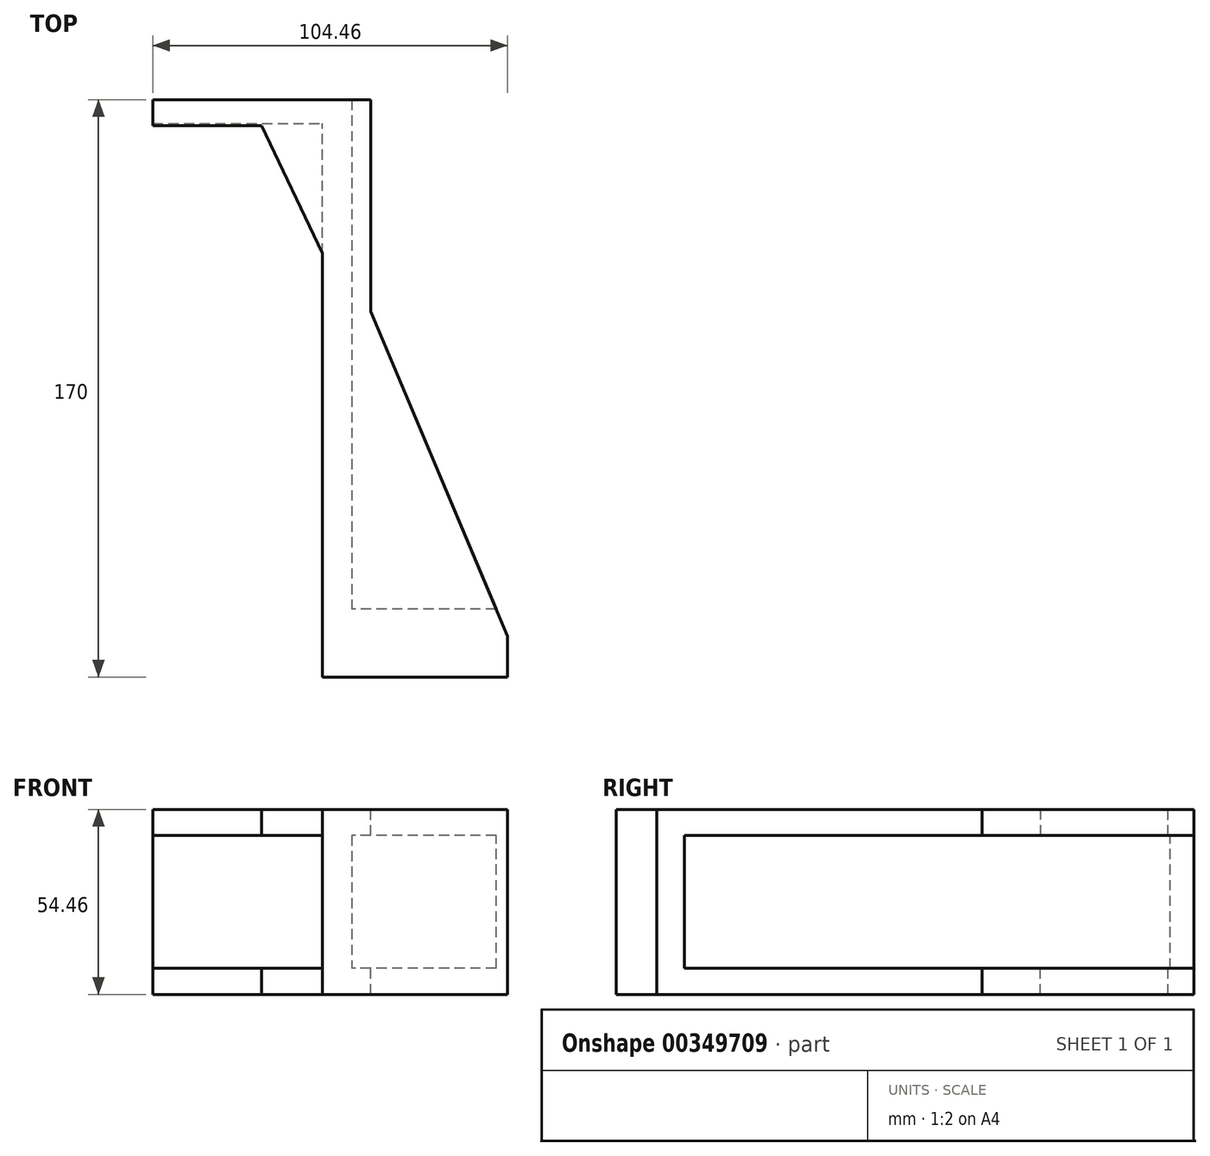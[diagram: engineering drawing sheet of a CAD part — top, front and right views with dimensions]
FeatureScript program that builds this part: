
annotation { "Feature Type Name" : "Feature", "Feature Type Description" : "" }
export const myFeature = defineFeature(function(context is Context, id is Id, definition is map)
    precondition{}
    {
        {
            var Q0;
            Q0=qCreatedBy(makeId("Front.planeOp"),FACE);
            var sketch = newSketch(context, id + "F0", { "sketchPlane" : qUnion([Q0])});
            skLineSegment(sketch, "E0", {"start": v(-28.4, 0) * mm, "end": v(-28.4, 27.23) * mm});
            skLineSegment(sketch, "E1", {"start": v(-28.4, 27.23) * mm, "end": v(26.05, 27.23) * mm});
            skLineSegment(sketch, "E2", {"start": v(26.05, 27.23) * mm, "end": v(26.05, 0) * mm});
            skLineSegment(sketch, "E3.MirrorCS", {"start": v(-28.4, 0) * mm, "end": v(-28.4, -27.23) * mm});
            skLineSegment(sketch, "E4.MirrorCS", {"start": v(-28.4, -27.23) * mm, "end": v(26.05, -27.23) * mm});
            skLineSegment(sketch, "E5.MirrorCS", {"start": v(26.05, -27.23) * mm, "end": v(26.05, 0) * mm});
            skSolve(sketch);
        }
        {
            var Q0;
            Q0 = qSketchRegion(id + "F0", true);
            extrude(context, id + "F1", {"entities" : qUnion([Q0]), "depth" : 20 * mm});
        }
        {
            var Q0;
            Q0=makeQuery(id+"F1.opExtrude","CAP_FACE",FACE,{"disambiguationData":[OSD([sQuery(id+"F0.wireOp",EDGE,"E0"),sQuery(id+"F0.wireOp",EDGE,"E1"),sQuery(id+"F0.wireOp",EDGE,"E2"),sQuery(id+"F0.wireOp",EDGE,"E3.MirrorCS"),sQuery(id+"F0.wireOp",EDGE,"E4.MirrorCS"),sQuery(id+"F0.wireOp",EDGE,"E5.MirrorCS")])],"isStart":true});
            var sketch = newSketch(context, id + "F2", { "sketchPlane" : qUnion([Q0])});
            skLineSegment(sketch, "E6.bottom", {"start": v(28.4, 27.23) * mm, "end": v(-26.05, 27.23) * mm});
            skLineSegment(sketch, "E6.top", {"start": v(28.4, -27.23) * mm, "end": v(-26.05, -27.23) * mm});
            skLineSegment(sketch, "E6.left", {"start": v(28.4, 27.23) * mm, "end": v(28.4, -27.23) * mm});
            skLineSegment(sketch, "E7", {"start": v(-26.05, 27.23) * mm, "end": v(-26.05, 19.58) * mm});
            skLineSegment(sketch, "E8", {"start": v(-26.05, 19.58) * mm, "end": v(19.87, 19.58) * mm});
            skLineSegment(sketch, "E9", {"start": v(19.87, 19.58) * mm, "end": v(19.87, 0) * mm});
            skLineSegment(sketch, "E10.MirrorCS", {"start": v(-26.05, -19.58) * mm, "end": v(19.87, -19.58) * mm});
            skLineSegment(sketch, "E11.MirrorCS", {"start": v(19.87, -19.58) * mm, "end": v(19.87, 0) * mm});
            skLineSegment(sketch, "E12.MirrorCS", {"start": v(-26.05, -27.23) * mm, "end": v(-26.05, -19.58) * mm});
            skSolve(sketch);
        }
        {
            var Q0;
            Q0 = qSketchRegion(id + "F2", true);
            extrude(context, id + "F3", {"entities" : qUnion([Q0]), "operationType" : NewBodyOperationType.ADD, "depth" : 150 * mm});
        }
        {
            var Q0;
            Q0=makeQuery(id+"F3.boolean.opBoolean","MERGE",FACE,{"derivedFrom":[makeQuery(id+"F1.opExtrude","SWEPT_FACE",FACE,{"disambiguationData":[OSD([sQuery(id+"F0.wireOp",EDGE,"E0"),sQuery(id+"F0.wireOp",EDGE,"E3.MirrorCS")])]}),makeQuery(id+"F3.opExtrude","SWEPT_FACE",FACE,{"disambiguationData":[OSD([sQuery(id+"F2.wireOp",EDGE,"E6.left")])]})]});
            var sketch = newSketch(context, id + "F4", { "sketchPlane" : qUnion([Q0])});
            skLineSegment(sketch, "E13", {"start": v(-150, 0) * mm, "end": v(-150, 27.23) * mm});
            skLineSegment(sketch, "E14", {"start": v(-150, 27.23) * mm, "end": v(-104.77, 27.23) * mm});
            skLineSegment(sketch, "E15", {"start": v(-104.77, 27.23) * mm, "end": v(-104.77, 19.58) * mm});
            skLineSegment(sketch, "E16", {"start": v(-104.77, 19.58) * mm, "end": v(-143.04, 19.58) * mm});
            skLineSegment(sketch, "E17", {"start": v(-143.04, 19.58) * mm, "end": v(-143.04, 0) * mm});
            skLineSegment(sketch, "E18.MirrorCS", {"start": v(-150, 0) * mm, "end": v(-150, -27.23) * mm});
            skLineSegment(sketch, "E19.MirrorCS", {"start": v(-150, -27.23) * mm, "end": v(-104.77, -27.23) * mm});
            skLineSegment(sketch, "E20.MirrorCS", {"start": v(-104.77, -27.23) * mm, "end": v(-104.77, -19.58) * mm});
            skLineSegment(sketch, "E21.MirrorCS", {"start": v(-104.77, -19.58) * mm, "end": v(-143.04, -19.58) * mm});
            skLineSegment(sketch, "E22.MirrorCS", {"start": v(-143.04, -19.58) * mm, "end": v(-143.04, 0) * mm});
            skSolve(sketch);
        }
        {
            var Q0;
            Q0 = qSketchRegion(id + "F4", true);
            extrude(context, id + "F5", {"entities" : qUnion([Q0]), "operationType" : NewBodyOperationType.ADD, "depth" : 50 * mm});
        }
        {
            var Q0;
            Q0=makeQuery(id+"F5.boolean.opBoolean","MERGE",FACE,{"derivedFrom":[makeQuery(id+"F3.boolean.opBoolean","MERGE",FACE,{"derivedFrom":[makeQuery(id+"F1.opExtrude","SWEPT_FACE",FACE,{"disambiguationData":[OSD([sQuery(id+"F0.wireOp",EDGE,"E1")])]}),makeQuery(id+"F3.opExtrude","SWEPT_FACE",FACE,{"disambiguationData":[OSD([sQuery(id+"F2.wireOp",EDGE,"E6.bottom")])]})]}),makeQuery(id+"F5.opExtrude","SWEPT_FACE",FACE,{"disambiguationData":[OSD([sQuery(id+"F4.wireOp",EDGE,"E14")])]})]});
            var sketch = newSketch(context, id + "F6", { "sketchPlane" : qUnion([Q0])});
            skLineSegment(sketch, "E23", {"start": v(26.05, -8.03) * mm, "end": v(26.05, 150) * mm});
            skLineSegment(sketch, "E24", {"start": v(26.05, 150) * mm, "end": v(-14.29, 150) * mm});
            skLineSegment(sketch, "E25", {"start": v(26.05, -8.03) * mm, "end": v(-14.29, 87.62) * mm});
            skLineSegment(sketch, "E26", {"start": v(-14.29, 87.62) * mm, "end": v(-14.29, 150) * mm});
            skSolve(sketch);
        }
        {
            var Q0;
            Q0 = qSketchRegion(id + "F6", true);
            extrude(context, id + "F7", {"entities" : qUnion([Q0]), "operationType" : NewBodyOperationType.REMOVE, "endBound" : BoundingType.THROUGH_ALL, "oppositeDirection" : true, "depth" : 25 * mm});
        }
        {
            var Q0;
            Q0=makeQuery(id+"F5.boolean.opBoolean","MERGE",FACE,{"derivedFrom":[makeQuery(id+"F3.boolean.opBoolean","MERGE",FACE,{"derivedFrom":[makeQuery(id+"F1.opExtrude","SWEPT_FACE",FACE,{"disambiguationData":[OSD([sQuery(id+"F0.wireOp",EDGE,"E1")])]}),makeQuery(id+"F3.opExtrude","SWEPT_FACE",FACE,{"disambiguationData":[OSD([sQuery(id+"F2.wireOp",EDGE,"E6.bottom")])]})]}),makeQuery(id+"F5.opExtrude","SWEPT_FACE",FACE,{"disambiguationData":[OSD([sQuery(id+"F4.wireOp",EDGE,"E14")])]})]});
            var sketch = newSketch(context, id + "F8", { "sketchPlane" : qUnion([Q0])});
            skLineSegment(sketch, "E27", {"start": v(-28.4, 104.77) * mm, "end": v(-46.35, 142.4) * mm});
            skPoint(sketch, "E27.endSnap0", {"position": v(-46.35, 150) * mm});
            skLineSegment(sketch, "E28", {"start": v(-46.35, 142.4) * mm, "end": v(-78.4, 142.4) * mm});
            skLineSegment(sketch, "E29", {"start": v(-78.4, 142.4) * mm, "end": v(-78.4, 104.77) * mm});
            skLineSegment(sketch, "E30", {"start": v(-78.4, 104.77) * mm, "end": v(-28.4, 104.77) * mm});
            skSolve(sketch);
        }
        {
            var Q0;
            Q0 = qSketchRegion(id + "F8", true);
            extrude(context, id + "F9", {"entities" : qUnion([Q0]), "operationType" : NewBodyOperationType.REMOVE, "endBound" : BoundingType.THROUGH_ALL, "oppositeDirection" : true, "depth" : 25 * mm});
        }
    });
